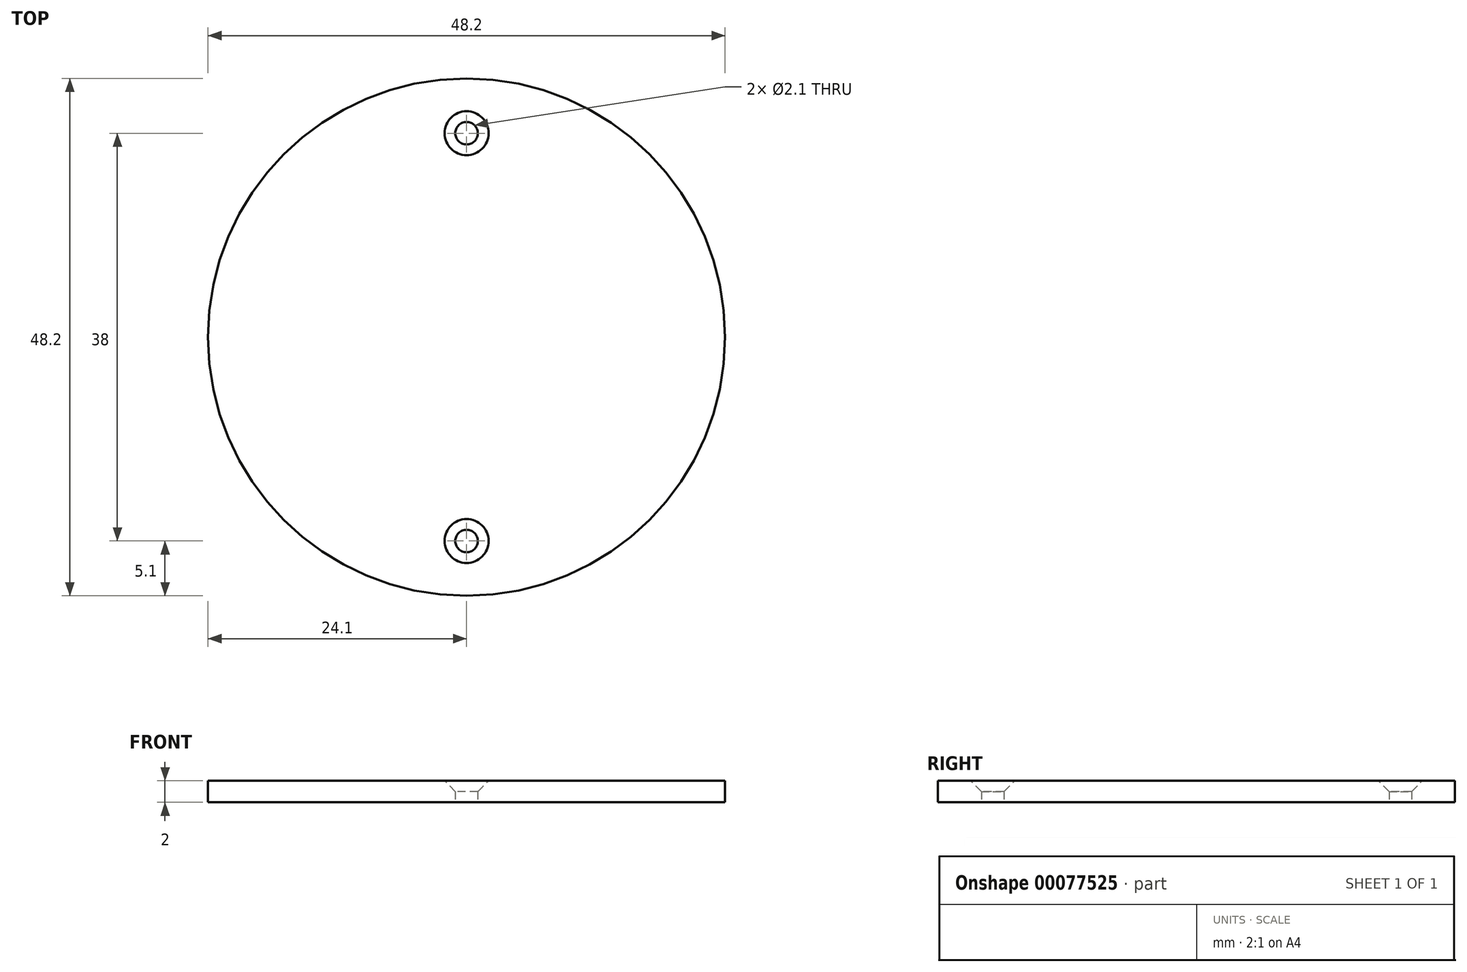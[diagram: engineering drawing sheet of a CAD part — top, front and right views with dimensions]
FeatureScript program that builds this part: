
annotation { "Feature Type Name" : "Feature", "Feature Type Description" : "" }
export const myFeature = defineFeature(function(context is Context, id is Id, definition is map)
    precondition{}
    {
        {
            var Q0;
            Q0=qCreatedBy(makeId("Top.planeOp"),FACE);
            var sketch = newSketch(context, id + "F0", { "sketchPlane" : qUnion([Q0])});
            skCircle(sketch, "E0", {"center": v(0, 0) * mm, "radius": 24.1 * mm});
            skCircle(sketch, "E1", {"center": v(0, 19) * mm, "radius": 1.05 * mm});
            skCircle(sketch, "E2", {"center": v(0, -19) * mm, "radius": 1.05 * mm});
            skSolve(sketch);
        }
        {
            var Q0;
            Q0=makeQuery(id+"F0.imprint","IMPRINT",FACE,{"disambiguationData":[TD([[makeQuery(id+"F0.imprint","IMPRINT",EDGE,{"derivedFrom":sQuery(id+"F0.wireOp",EDGE,"E0")}),1.0]])]});
            extrude(context, id + "F1", {"entities" : qUnion([Q0]), "depth" : 2 * mm});
        }
        {
            var Q0;
            Q0=makeQuery(id+"F1.opExtrude","CAP_EDGE",EDGE,{"disambiguationData":[OSD([sQuery(id+"F0.wireOp",EDGE,"E1")])],"isStart":false});
            var Q1;
            Q1=makeQuery(id+"F1.opExtrude","CAP_EDGE",EDGE,{"disambiguationData":[OSD([sQuery(id+"F0.wireOp",EDGE,"E2")])],"isStart":false});
            chamfer(context, id + "F2", {"entities" : qUnion([Q0, Q1]), "width" : 1 * mm, "tangentPropagation" : true});
        }
    });
